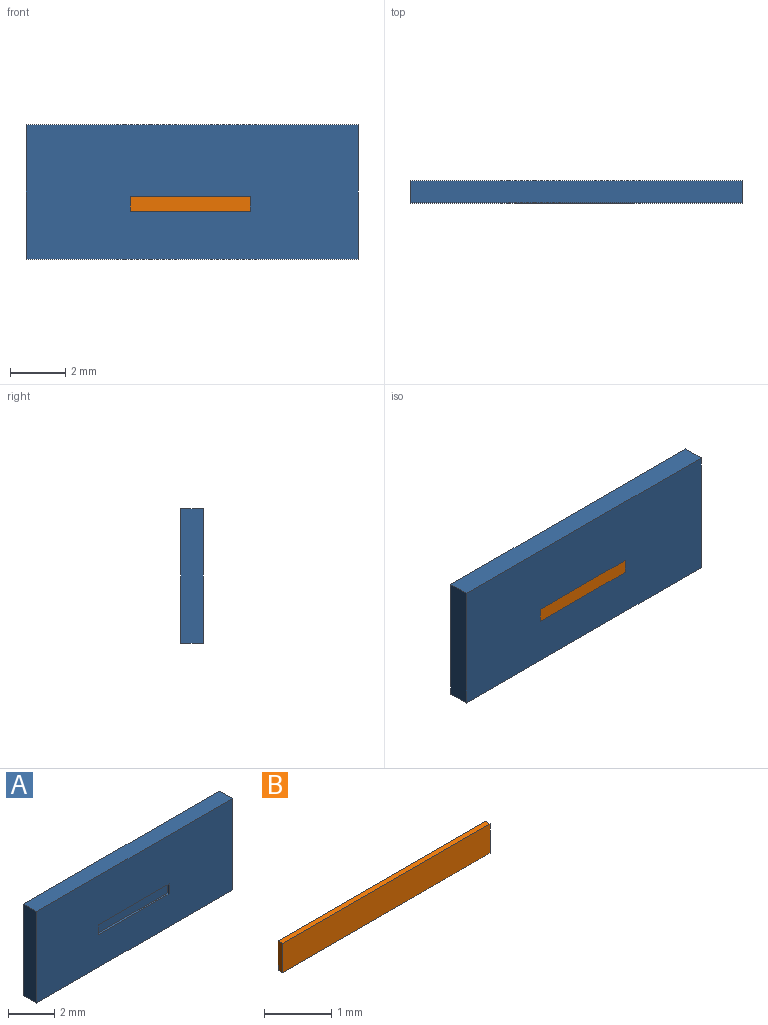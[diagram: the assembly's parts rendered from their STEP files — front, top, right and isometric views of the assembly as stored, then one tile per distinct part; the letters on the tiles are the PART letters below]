
ASSEMBLY  parts=2 mates=1
PART A: 11 faces, bbox 12x0.8x4.9 mm
  f0: plane 12x4.85mm, normal (0,-1,0), area 55.9mm2, adj f1,f2,f3,f4,f6,f7,f8,f9
  f1: plane 12x0.8mm, normal (0,0,-1), area 9.6mm2, adj f0,f2,f4,f5
  f2: plane 4.85x0.8mm, normal (1,0,0), area 3.9mm2, adj f0,f1,f3,f5
  f3: plane 12x0.8mm, normal (0,0,1), area 9.6mm2, adj f0,f2,f4,f5
  f4: plane 4.85x0.8mm, normal (-1,0,0), area 3.9mm2, adj f0,f1,f3,f5
  f5: plane 12x4.85mm, normal (0,1,0), area 58.2mm2, adj f1,f2,f3,f4
  f6: plane 4.34x0.1mm, normal (0,0,1), area 0.4mm2, adj f0,f7,f9,f10
  f7: plane 0.53x0.1mm, normal (-1,0,0), area 0.1mm2, adj f0,f6,f8,f10
  f8: plane 4.34x0.1mm, normal (0,0,-1), area 0.4mm2, adj f0,f7,f9,f10
  f9: plane 0.53x0.1mm, normal (1,0,0), area 0.1mm2, adj f0,f6,f8,f10
  f10: plane 4.34x0.53mm, normal (0,-1,0), area 2.3mm2, adj f6,f7,f8,f9
PART B: 6 faces, bbox 4.3x0.1x0.5 mm
  f0: plane 4.34x0.53mm, normal (0,-1,0), area 2.3mm2, adj f1,f3,f4,f5
  f1: plane 0.53x0.1mm, normal (1,0,0), area 0.1mm2, adj f0,f2,f3,f4
  f2: plane 4.34x0.53mm, normal (0,1,0), area 2.3mm2, adj f1,f3,f4,f5
  f3: plane 4.34x0.1mm, normal (0,0,1), area 0.4mm2, adj f0,f1,f2,f5
  f4: plane 4.34x0.1mm, normal (0,0,-1), area 0.4mm2, adj f0,f1,f2,f5
  f5: plane 0.53x0.1mm, normal (-1,0,0), area 0.1mm2, adj f0,f2,f3,f4
PLACE A t=(0.02,0.38,-0.05)mm
PLACE B t=(0.02,0.38,-0.05)mm
MATE fastened B.f0 <-> A.f0  axis (0,-1,0) through (-2.21,-0.42,-0.74)mm
